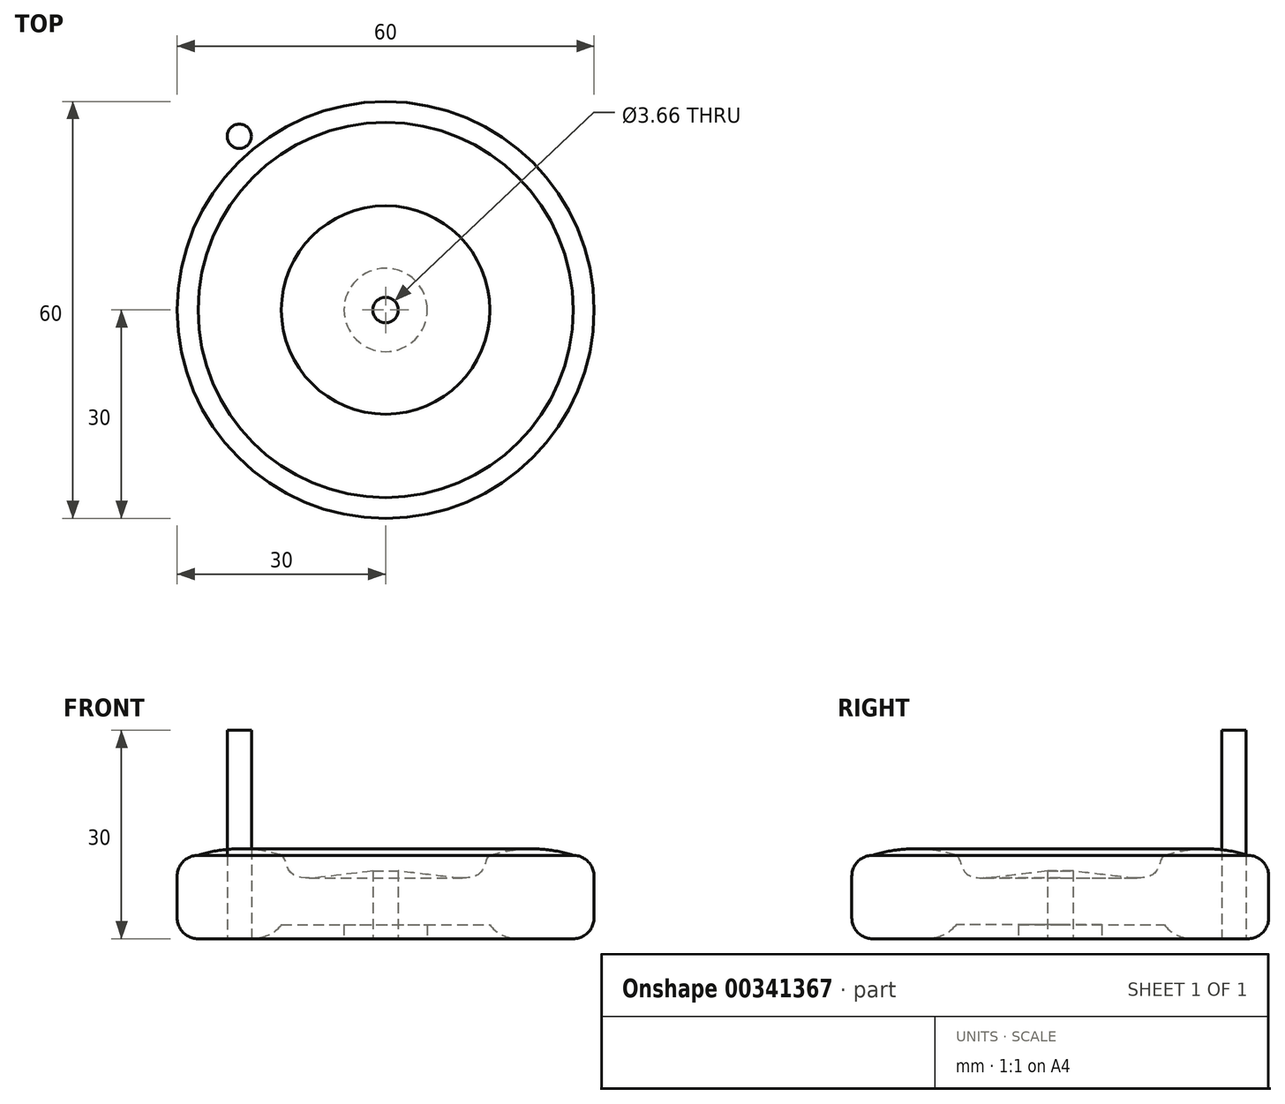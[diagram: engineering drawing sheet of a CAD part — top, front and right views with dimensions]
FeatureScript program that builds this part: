
annotation { "Feature Type Name" : "Feature", "Feature Type Description" : "" }
export const myFeature = defineFeature(function(context is Context, id is Id, definition is map)
    precondition{}
    {
        {
            var Q0;
            Q0=qCreatedBy(makeId("Top.planeOp"),FACE);
            var sketch = newSketch(context, id + "F0", { "sketchPlane" : qUnion([Q0])});
            skCircle(sketch, "E0", {"center": v(-21.06, 25) * mm, "radius": 1.75 * mm});
            skSolve(sketch);
        }
        {
            var Q0;
            Q0=makeQuery(id+"F0.imprint","IMPRINT",FACE,{"disambiguationData":[TD([[makeQuery(id+"F0.imprint","IMPRINT",EDGE,{"derivedFrom":sQuery(id+"F0.wireOp",EDGE,"E0")}),1.0]])]});
            extrude(context, id + "F1", {"entities" : qUnion([Q0]), "depth" : 30 * mm});
        }
        {
            var Q0;
            Q0=qCreatedBy(makeId("Front.planeOp"),FACE);
            var sketch = newSketch(context, id + "F2", { "sketchPlane" : qUnion([Q0])});
            skLineSegment(sketch, "E1", {"start": v(0, 0) * mm, "end": v(0, 10) * mm});
            skLineSegment(sketch, "E2", {"start": v(30, 9) * mm, "end": v(30, 3) * mm});
            skLineSegment(sketch, "E3", {"start": v(27, 0) * mm, "end": v(15, 0) * mm});
            skLineSegment(sketch, "E4", {"start": v(15, 0) * mm, "end": v(15, 2) * mm});
            skLineSegment(sketch, "E5", {"start": v(15, 2) * mm, "end": v(6, 2) * mm});
            skLineSegment(sketch, "E6", {"start": v(6, 2) * mm, "end": v(6, 0) * mm});
            skPoint(sketch, "E7.visualSharp", {"position": v(30, 0) * mm});
            skArc(sketch, "E7.filletArc", {"start": v(27, 0) * mm, "mid": v(29.12, 0.88) * mm, "end": v(30, 3) * mm});
            skPoint(sketch, "E8.visualSharp", {"position": v(30, 10) * mm});
            skArc(sketch, "E8.filletArc", {"start": v(30, 9) * mm, "mid": v(29.12, 11.12) * mm, "end": v(27, 12) * mm});
            skArc(sketch, "E9", {"start": v(27, 12) * mm, "mid": v(21, 12.93) * mm, "end": v(15, 12) * mm});
            skPoint(sketch, "E10.visualSharp", {"position": v(15, 0) * mm});
            skFitSpline(sketch, "E11", {"points": [v(0, 10) * mm, v(8, 9) * mm, v(13.65, 9.53) * mm, v(15, 12) * mm], "startDerivative": vector(24.02, -3.4) * mm, "endDerivative": vector(6.99, 1.38) * mm});
            skLineSegment(sketch, "E12", {"start": v(0, 0) * mm, "end": v(6, 0) * mm});
            skSolve(sketch);
        }
        {
            var Q0;
            Q0=makeQuery(id+"F2.imprint","IMPRINT",FACE,{"disambiguationData":[TD([[makeQuery(id+"F2.imprint","IMPRINT",EDGE,{"derivedFrom":sQuery(id+"F2.wireOp",EDGE,"E1")}),-1.0]])]});
            var Q1;
            Q1=sQuery(id+"F2.wireOp",EDGE,"E1");
            revolve(context, id + "F3", {"entities" : qUnion([Q0]), "axis" : qUnion([Q1]), "revolveType" : RevolveType.FULL});
        }
        {
            var Q0;
            Q0=makeQuery(id+"F3.opRevolve","SWEPT_EDGE",EDGE,{"disambiguationData":[OSD([sQuery(id+"F2.wireOp",EDGE,"E3"),sQuery(id+"F2.wireOp",EDGE,"E4")])]});
            fillet(context, id + "F4", {"entities" : qUnion([Q0]), "radius" : 5 * mm, "tangentPropagation" : true, "allowEdgeOverflow" : false});
        }
        {
            var Q0;
            Q0=qCreatedBy(makeId("Top.planeOp"),FACE);
            var sketch = newSketch(context, id + "F5", { "sketchPlane" : qUnion([Q0])});
            skPoint(sketch, "E13", {"position": v(0, 0) * mm});
            skSolve(sketch);
        }
        {
            var Q0;
            Q0=sQuery(id+"F5.wireOp",VERTEX,"E13");
            var Q1;
            Q1=makeQuery(id+"F3.opRevolve","SWEPT_BODY",BODY,{"disambiguationData":[OSD([sQuery(id+"F2.wireOp",EDGE,"E1"),sQuery(id+"F2.wireOp",EDGE,"E2"),sQuery(id+"F2.wireOp",EDGE,"E3"),sQuery(id+"F2.wireOp",EDGE,"E4"),sQuery(id+"F2.wireOp",EDGE,"E5"),sQuery(id+"F2.wireOp",EDGE,"E6"),sQuery(id+"F2.wireOp",EDGE,"Q9cDsmCs-q79E-soxS-GJNm-XGcUUAOyhzII"),sQuery(id+"F2.wireOp",EDGE,"E7.filletArc"),sQuery(id+"F2.wireOp",EDGE,"E8.filletArc"),sQuery(id+"F2.wireOp",EDGE,"E9"),sQuery(id+"F2.wireOp",EDGE,"E11")])]});
            hole(context, id + "F6", {"style" : HoleStyle.SIMPLE, "endStyle" : HoleEndStyle.THROUGH, "oppositeDirection" : true, "standardTappedOrClearance" : lookupTablePath({ "standard" : "ANSI", "fit" : "Close", "size" : "#6", "type" : "Clearance" }), "standardBlindInLast" : lookupTablePath({ "fit" : "Close", "standard" : "ANSI", "size" : "#6", "type" : "Clearance" }), "holeDiameter" : 3.66 * mm, "startFromSketch" : true, "locations" : qUnion([Q0]), "scope" : qUnion([Q1]), "isTappedThrough" : true});
        }
    });
